# Revit family: IS_Conca_T4354_BIM_IT
name_source: partatom
category: Plumbing Fixtures
revit_build: Autodesk Revit 2017 (Build: 20160225_1515(x64)
units: mm (PartAtom-declared; Revit-internal decimal feet)

## family parameters
Always vertical = No
Cut with Voids When Loaded = No
OmniClass Number = 23.45.05.14.21.11
OmniClass Title = Bath/Shower Units
Part Type = Normal
Room Calculation Point = No
Round Connector Dimension = Use Diameter
Shared = No
Work Plane-Based = No

## types (6) — shared parameters
Accessori = https://www.idealstandard.it
Aiuto = https://www.idealstandard.it
Autore = Ideal Standard
BIMobject category = Storage
BIMobject category code = sanitary-storage
BIMobject main category = Sanitary
BIMobject main category code = sanitary
Brand = https://www.idealstandard.it
Brand url = http://www.idealstandard.co.uk
DescrizioneClassifcazioneUni2015 = Bathroom cabinets
DurataGaranzia = 2
DurataGaranziaProdotti = 2
Edition number = 1
Forma = Rettangolare
Garanzia = Garanzia Idealstandard
IFC Classification = Sanitary Terminal
IfcEsportaCome = IfcFurnitureType
InformaziniGaranzia = https://www.idealstandard.it
InformazioniDiProdotto = http://www.idealstandard.it
InformazioniGaranzia = https://www.idealstandard.it
Installation instructions = https://www.idealspec.co.uk
InstruzioniInstallazione = https://www.idealstandard.it
Maniglia = No
Manufacturer = Ideal Standard
Manufacturer name = Ideal Standard
Masterformat 2014 Code = 12 50 00
Masterformat 2014 Description = Furniture
Material main = MDF
Materiale = Ceramics
NBS Reference Code = 45-35-72/318
NBS Reference Description = Bathroom cabinets
NominalDepth = 373 mm  [stored 1.22375 ft]
NominalHeight = 539 mm
NominalWidth = 600 mm
OmniClass Code = 23-31 25 13
OmniClass Description = Bathroom Cabinets
PiattoDoccia = No
Product Guid = bcab852e-c8cd-4bfd-9915-7353f1978c5a
Product SKU = T4354
Product data url = https://bimobject.com
Product family = Conca
Product group = Bathroom_Furniture
Product url = https://www.ideal-standard.co.uk
Produttore = Ideal Standard
QR code = http://bimobject.com
Revisione = 1
RiferimentoClassificazioneUni2015 = Pr_40_30_78_03
Spazio = Interno
Technical description = https://www.idealspec.co.uk
Telefono = 800 652 290
TipoEspotazioneIfc = Bathroom cabinets
UNSPSC Code = 301815
URL = https://www.ideal-standard.co.uk
Uniclass 1.4 Code = L8241
Uniclass 1.4 Description = Bathroom cabinets
Uniclass 2.0 Code = PR-35-75-08
Uniclass 2.0 Description = Bathroom Cabinets
Uniclass 2015 Code = Pr_40_30_78_03
Uniclass 2015 Name = Bathroom cabinets
UnitàDurata = Anno
UnitàDurataGaranzia = Anno
UnitàLineare = Milimitre
UnitàMonetaria = €
UnitàSuperficie = Milimitre
UnitàVolume = Litri
Versione = 1
VersioneClassificazioneUni2015 = v1.1
zero-valued in all types: CostoDiSostituzione, DimensioneScarico, LunghezzaNominale, Nominal depth, Nominal height, NominalLength, SeatMaterial, SpessoreDelMateriale, SpilloverLivello, Weight Net (Kg)

## per-type parameters (varying)
| type | AltezzaNominale | Caratteristiche | CodiceABarre | CodiceArticolo | Colore | Description | Desrizione | Finitura | GTIN code | LarghezzaNominale | Model | ModelNumber | ModelloDiRiferimento | NettWeight | Nome | NomeOggettoBim | NumeroDiModello | PesoNetto | Product name | ProfonditaNominale |
| T4354Y1 - BSN UN 60X37X55 2 DR NOWTOP WHMT | 0 mm  [stored 0 ft] | Mobile sottolavabo, 600 x 372 x 550mm  senza piano da appoggio per l'abbinamento ai piani in gres porcellanato o alle mensole  con 2 cassetti esterni. Dotato di tecnologia push open e soft close. Cassetti in metallo . Finitura Bianco laccato opaco | 8014140465669 | T4354Y1 | Matt white | Vanity unit, 600 x 372 x 550mm without countertop to combine with porcelain stoneware tops or shelves with 2 external drawers. Equipped with push open and soft close technology.  Matt white lacquered finish | Mobile sottolavabo, 600 x 372 x 550mm  senza piano da appoggio per l'abbinamento ai piani in gres porcellanato o alle mensole  con 2 cassetti esterni. Dotato di tecnologia push open e soft close. Cassetti in metallo . Finitura Bianco laccato opaco | Matt white | https://8014140465669 | 0 mm  [stored 0 ft] | T4354Y1 | T4354Y1 | T4354Y1 | 0 | BathroomCabinets_Conca_T4354Y1_IdealStandard | ISI_IdealStandard_Bathroom Cabinets_Conca_T4354Y1 | T4354Y1 | 0 | Conca BSN UN 60X37X55 2 DR NOWTOP WHMT | 0 mm  [stored 0 ft] |
| T4354Y2 - BSN UN 60X37X55 2 DR NOWTOP ANMT | 550 mm | Mobile sottolavabo, 600 x 372 x 550mm  senza piano da appoggio per l'abbinamento ai piani in gres porcellanato o alle mensole  con 2 cassetti esterni. Dotato di tecnologia push open e soft close.Cassetti in metallo. Finitura Antracite laccato opaco | 8014140465676 | T4354Y2 | Matt anthracite | Vanity unit, 600 x 372 x 550mm without countertop to combine with porcelain stoneware tops or shelves with 2 external drawers. Equipped with push open and soft close technology. Metal trays. Anthracite matt lacquer finish | Mobile sottolavabo, 600 x 372 x 550mm  senza piano da appoggio per l'abbinamento ai piani in gres porcellanato o alle mensole  con 2 cassetti esterni. Dotato di tecnologia push open e soft close.Cassetti in metallo. Finitura Antracite laccato opaco | Matt anthracite | https://8014140465676 | 600 mm | T4354Y2 | T4354Y2 | T4354Y2 | 27.5 | BathroomCabinets_Conca_T4354Y2_IdealStandard | ISI_IdealStandard_Bathroom Cabinets_Conca_T4354Y2 | T4354Y2 | 27.5 | Conca BSN UN 60X37X55 2 DR NOWTOP ANMT | 372 mm  [stored 1.22047 ft] |
| T4354Y3 - BSN UN 60X37X55 2 DR NOWTOP SNMT | 550 mm | Mobile sottolavabo, 600 x 372 x 550mm  senza piano da appoggio per l'abbinamento ai piani in gres porcellanato o alle mensole  con 2 cassetti esterni. Dotato di tecnologia push open e soft close.Cassetti in metallo. Finitura Sunset laccato opaco | 8014140465683 | T4354Y3 | Matt Sunset | Vanity unit, 600 x 372 x 550mm without countertop to combine with porcelain stoneware tops or shelves with 2 external drawers. Equipped with push open and soft close technology. Metal trays. Sunset matt lacquer finish | Mobile sottolavabo, 600 x 372 x 550mm  senza piano da appoggio per l'abbinamento ai piani in gres porcellanato o alle mensole  con 2 cassetti esterni. Dotato di tecnologia push open e soft close.Cassetti in metallo. Finitura Sunset laccato opaco | Matt Sunset | https://8014140465683 | 600 mm | T4354Y3 | T4354Y3 | T4354Y3 | 27.5 | BathroomCabinets_Conca_T4354Y3_IdealStandard | ISI_IdealStandard_Bathroom Cabinets_Conca_T4354Y3 | T4354Y3 | 27.5 | Conca BSN UN 60X37X55 2 DR NOWTOP SNMT | 372 mm  [stored 1.22047 ft] |
| T4354Y4 - BSN UN 60X37X55 2 DR NOWTOP SMOK | 550 mm | Mobile sottolavabo, 600 x 372 x 550mm  senza piano da appoggio per l'abbinamento ai piani in gres porcellanato o alle mensole  con 2 cassetti esterni. Dotato di tecnologia push open e soft close.Cassetti in metallo. Finitura Rovere affumicato scuro | 8014140465690 | T4354Y4 | Smoked Oak | Vanity unit, 600 x 372 x 550mm without countertop to combine with porcelain stoneware tops or shelves with 2 external drawers. Equipped with push open and soft close technology. Metal trays. Dark smoked oak finish | Mobile sottolavabo, 600 x 372 x 550mm  senza piano da appoggio per l'abbinamento ai piani in gres porcellanato o alle mensole  con 2 cassetti esterni. Dotato di tecnologia push open e soft close.Cassetti in metallo. Finitura Rovere affumicato scuro | Smoked Oak | https://8014140465690 | 600 mm | T4354Y4 | T4354Y4 | T4354Y4 | 27.5 | BathroomCabinets_Conca_T4354Y4_IdealStandard | ISI_IdealStandard_Bathroom Cabinets_Conca_T4354Y4 | T4354Y4 | 27.5 | Conca BSN UN 60X37X55 2 DR NOWTOP SMOK | 372 mm  [stored 1.22047 ft] |
| T4354Y5 - BSN UN 60X37X55 2 DR NOWTOP DKWN | 550 mm | Mobile sottolavabo, 600 x 372 x 550mm  senza piano da appoggio per l'abbinamento ai piani in gres porcellanato o alle mensole  con 2 cassetti esterni. Dotato di tecnologia push open e soft close. Cassetti in metallo. Finitura Noce scuro | 8014140465706 | T4354Y5 | Dark Walnut | Vanity unit, 600 x 372 x 550mm without countertop to combine with porcelain stoneware tops or shelves with 2 external drawers. Equipped with push open and soft close technology.  Dark Walnut finish | Mobile sottolavabo, 600 x 372 x 550mm  senza piano da appoggio per l'abbinamento ai piani in gres porcellanato o alle mensole  con 2 cassetti esterni. Dotato di tecnologia push open e soft close. Cassetti in metallo. Finitura Noce scuro | Dark Walnut | https://8014140465706 | 600 mm | T4354Y5 | T4354Y5 | T4354Y5 | 27.5 | BathroomCabinets_Conca_T4354Y5_IdealStandard | ISI_IdealStandard_Bathroom Cabinets_Conca_T4354Y5 | T4354Y5 | 27.5 | Conca BSN UN 60X37X55 2 DR NOWTOP DKWN | 372 mm  [stored 1.22047 ft] |
| T4354Y6 - BSN UN 60X37X55 2 DR NOWTOP LTOK | 550 mm | Mobile sottolavabo, 600 x 372 x 550mm  senza piano da appoggio per l'abbinamento ai piani in gres porcellanato o alle mensole  con 2 cassetti esterni. Dotato di tecnologia push open e soft close.Cassetti in metallo. Finitura Legno chiaro | 8014140465713 | T4354Y6 | Light Oak | Vanity unit, 600 x 372 x 550mm without countertop to combine with porcelain stoneware tops or shelves with 2 external drawers. Equipped with push open and soft close technology. Metal trays. Light wood finish | Mobile sottolavabo, 600 x 372 x 550mm  senza piano da appoggio per l'abbinamento ai piani in gres porcellanato o alle mensole  con 2 cassetti esterni. Dotato di tecnologia push open e soft close.Cassetti in metallo. Finitura Legno chiaro | Light Oak | https://8014140465713 | 600 mm | T4354Y6 | T4354Y6 | T4354Y6 | 27.5 | BathroomCabinets_Conca_T4354Y6_IdealStandard | ISI_IdealStandard_Bathroom Cabinets_Conca_T4354Y6 | T4354Y6 | 27.5 | Conca BSN UN 60X37X55 2 DR NOWTOP LTOK | 372 mm  [stored 1.22047 ft] |

note: [stored X ft] marks values corroborated as IEEE doubles in the binary element streams (Revit-internal decimal feet)

## geometry (parser evidence)
native form markers: Sweep x3
no freeform markers — native parametric forms only
